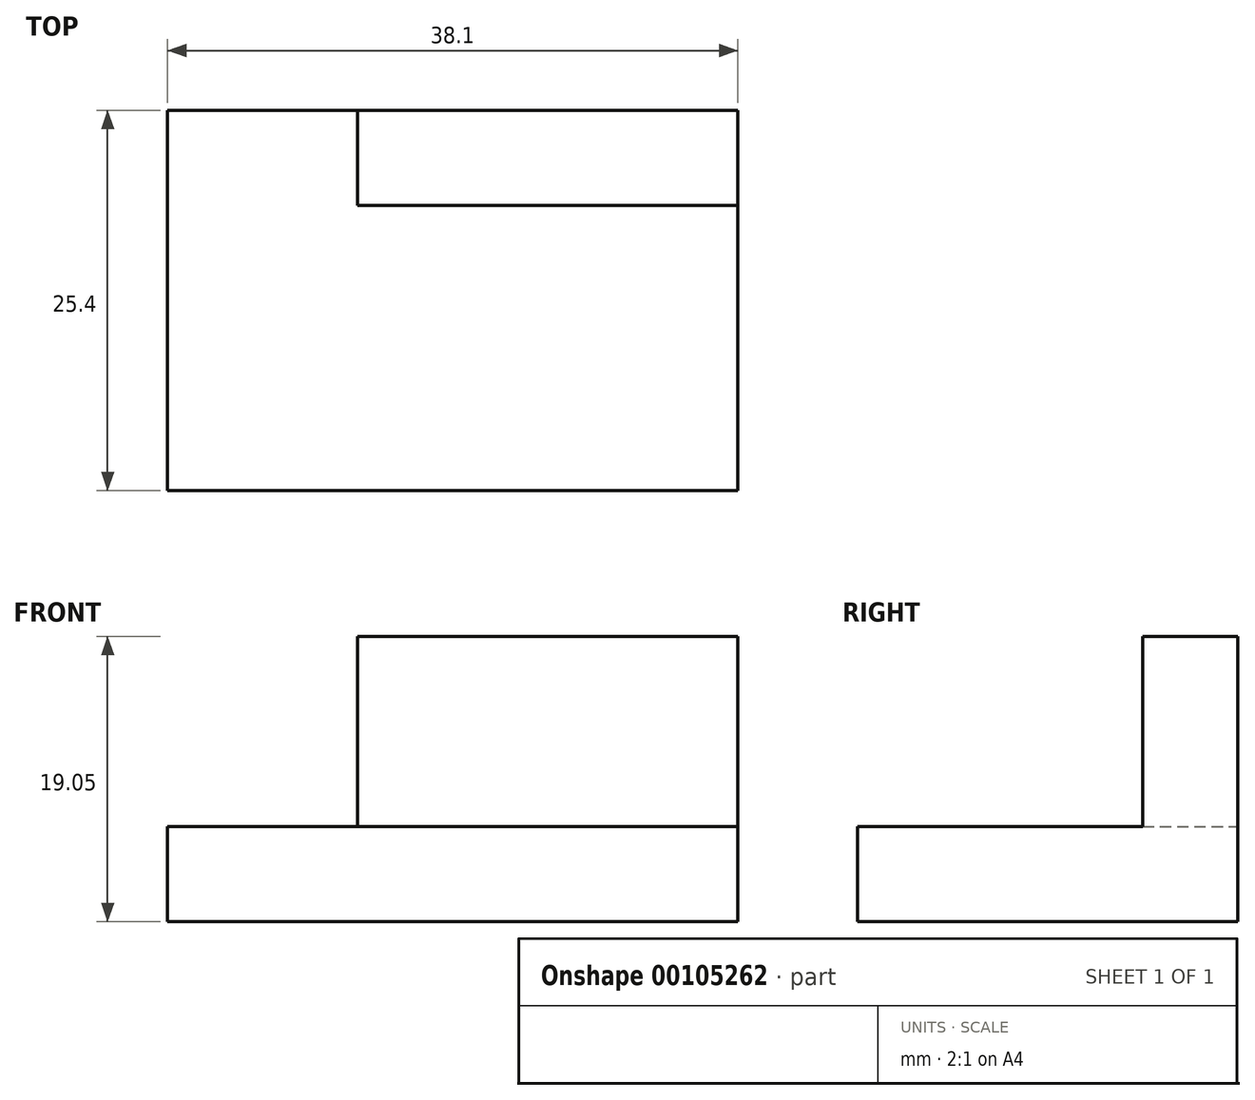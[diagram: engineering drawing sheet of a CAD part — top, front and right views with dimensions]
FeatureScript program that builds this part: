
annotation { "Feature Type Name" : "Feature", "Feature Type Description" : "" }
export const myFeature = defineFeature(function(context is Context, id is Id, definition is map)
    precondition{}
    {
        {
            var Q0;
            Q0=qCreatedBy(makeId("Front.planeOp"),FACE);
            var sketch = newSketch(context, id + "F0", { "sketchPlane" : qUnion([Q0])});
            skLineSegment(sketch, "E0.bottom", {"start": v(0, 0) * mm, "end": v(38.1, 0) * mm});
            skLineSegment(sketch, "E0.top", {"start": v(0, 6.35) * mm, "end": v(38.1, 6.35) * mm});
            skLineSegment(sketch, "E0.left", {"start": v(0, 0) * mm, "end": v(0, 6.35) * mm});
            skLineSegment(sketch, "E0.right", {"start": v(38.1, 0) * mm, "end": v(38.1, 6.35) * mm});
            skLineSegment(sketch, "E1.bottom", {"start": v(0, 6.35) * mm, "end": v(12.7, 6.35) * mm});
            skLineSegment(sketch, "E1.top", {"start": v(0, 25.4) * mm, "end": v(12.7, 25.4) * mm});
            skLineSegment(sketch, "E1.left", {"start": v(0, 6.35) * mm, "end": v(0, 25.4) * mm});
            skLineSegment(sketch, "E1.right", {"start": v(12.7, 6.35) * mm, "end": v(12.7, 25.4) * mm});
            skLineSegment(sketch, "E2.bottom", {"start": v(12.7, 19.05) * mm, "end": v(38.1, 19.05) * mm});
            skLineSegment(sketch, "E2.top", {"start": v(12.7, 6.35) * mm, "end": v(38.1, 6.35) * mm});
            skLineSegment(sketch, "E2.left", {"start": v(12.7, 19.05) * mm, "end": v(12.7, 6.35) * mm});
            skLineSegment(sketch, "E2.right", {"start": v(38.1, 19.05) * mm, "end": v(38.1, 6.35) * mm});
            skSolve(sketch);
        }
        {
            var Q0;
            Q0=makeQuery(id+"F0.imprint","IMPRINT",FACE,{"disambiguationData":[TD([[makeQuery(id+"F0.imprint","IMPRINT",EDGE,{"derivedFrom":sQuery(id+"F0.wireOp",EDGE,"E0.bottom")}),1.0]])]});
            var Q1;
            Q1=makeQuery(id+"F0.imprint","IMPRINT",FACE,{"disambiguationData":[TD([[makeQuery(id+"F0.imprint","IMPRINT",EDGE,{"derivedFrom":sQuery(id+"F0.wireOp",EDGE,"E1.bottom")}),1.0]])]});
            extrude(context, id + "F1", {"entities" : qUnion([Q0, Q1]), "depth" : 25.4 * mm});
        }
        {
            var Q0;
            Q0=makeQuery(id+"F0.imprint","IMPRINT",FACE,{"disambiguationData":[TD([[makeQuery(id+"F0.imprint","IMPRINT",EDGE,{"derivedFrom":sQuery(id+"F0.wireOp",EDGE,"E2.bottom")}),-1.0]])]});
            extrude(context, id + "F2", {"entities" : qUnion([Q0]), "operationType" : NewBodyOperationType.ADD, "depth" : 6.35 * mm});
        }
    });
